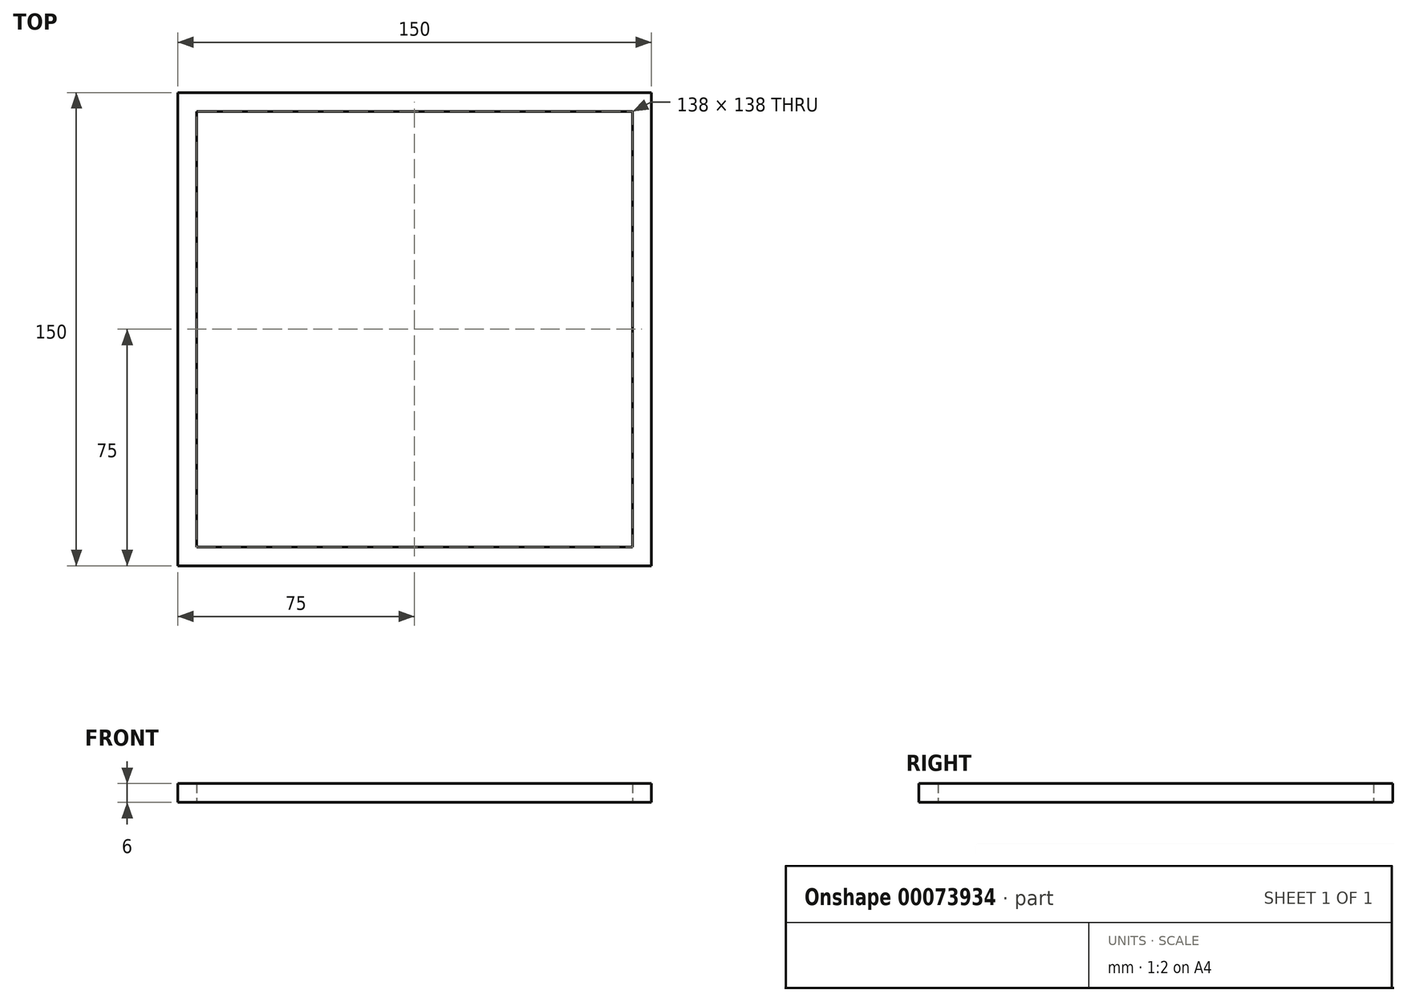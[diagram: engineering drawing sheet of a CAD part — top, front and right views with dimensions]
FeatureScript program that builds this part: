
annotation { "Feature Type Name" : "Feature", "Feature Type Description" : "" }
export const myFeature = defineFeature(function(context is Context, id is Id, definition is map)
    precondition{}
    {
        {
            var Q0;
            Q0=qCreatedBy(makeId("Top.planeOp"),FACE);
            var sketch = newSketch(context, id + "F0", { "sketchPlane" : qUnion([Q0])});
            skLineSegment(sketch, "E0.rect.bottom", {"start": v(75, 75) * mm, "end": v(-75, 75) * mm});
            skLineSegment(sketch, "E0.rect.top", {"start": v(75, -75) * mm, "end": v(-75, -75) * mm});
            skLineSegment(sketch, "E0.rect.left", {"start": v(75, 75) * mm, "end": v(75, -75) * mm});
            skLineSegment(sketch, "E0.rect.right", {"start": v(-75, 75) * mm, "end": v(-75, -75) * mm});
            skPoint(sketch, "E0.rect.middle", {"position": v(0, 0) * mm});
            skLineSegment(sketch, "E1.rect.bottom", {"start": v(69, 69) * mm, "end": v(-69, 69) * mm});
            skLineSegment(sketch, "E1.rect.top", {"start": v(69, -69) * mm, "end": v(-69, -69) * mm});
            skLineSegment(sketch, "E1.rect.left", {"start": v(69, 69) * mm, "end": v(69, -69) * mm});
            skLineSegment(sketch, "E1.rect.right", {"start": v(-69, 69) * mm, "end": v(-69, -69) * mm});
            skSolve(sketch);
        }
        {
            var Q0;
            Q0 = qSketchRegion(id + "F0", true);
            extrude(context, id + "F1", {"entities" : qUnion([Q0]), "depth" : 6 * mm});
        }
    });
